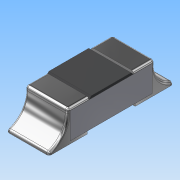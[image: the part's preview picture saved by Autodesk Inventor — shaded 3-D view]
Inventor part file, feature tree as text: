
AUTODESK INVENTOR PART (.ipt)
format: ipt  version: 2016 (Build 200138000, 138)  size: 206,336 bytes
history: native  units: mm
features: extrude x2, fillet x2, sketch x1, mirror x1
ambient origin geometry x8: Origin, YZ Plane, XZ Plane, XY Plane, X Axis, Y Axis, Z Axis, Center Point
bodies: Body1 (feature_tree)
feature tree (6):
  sketch  "Sketch10"  dims[d9=0.499mm d10=0.0mm d11=0.2mm d12=0.45mm d13=0.03mm d14=0.03mm d15=0.25mm d16=45.0deg d17=0.5mm d18=0.0mm d19=0.03mm d21=1.0mm d22=0.37mm d23=0.3mm d24=0.029mm]
  extrude  "Extrusion4"  Depth=0.2mm
  extrude  "Extrusion5"  Depth=0.45mm
  fillet  "Fillet2"  Radius=0.03mm
  fillet  "Fillet3"  Radius=0.03mm
  mirror  "Mirror1"
